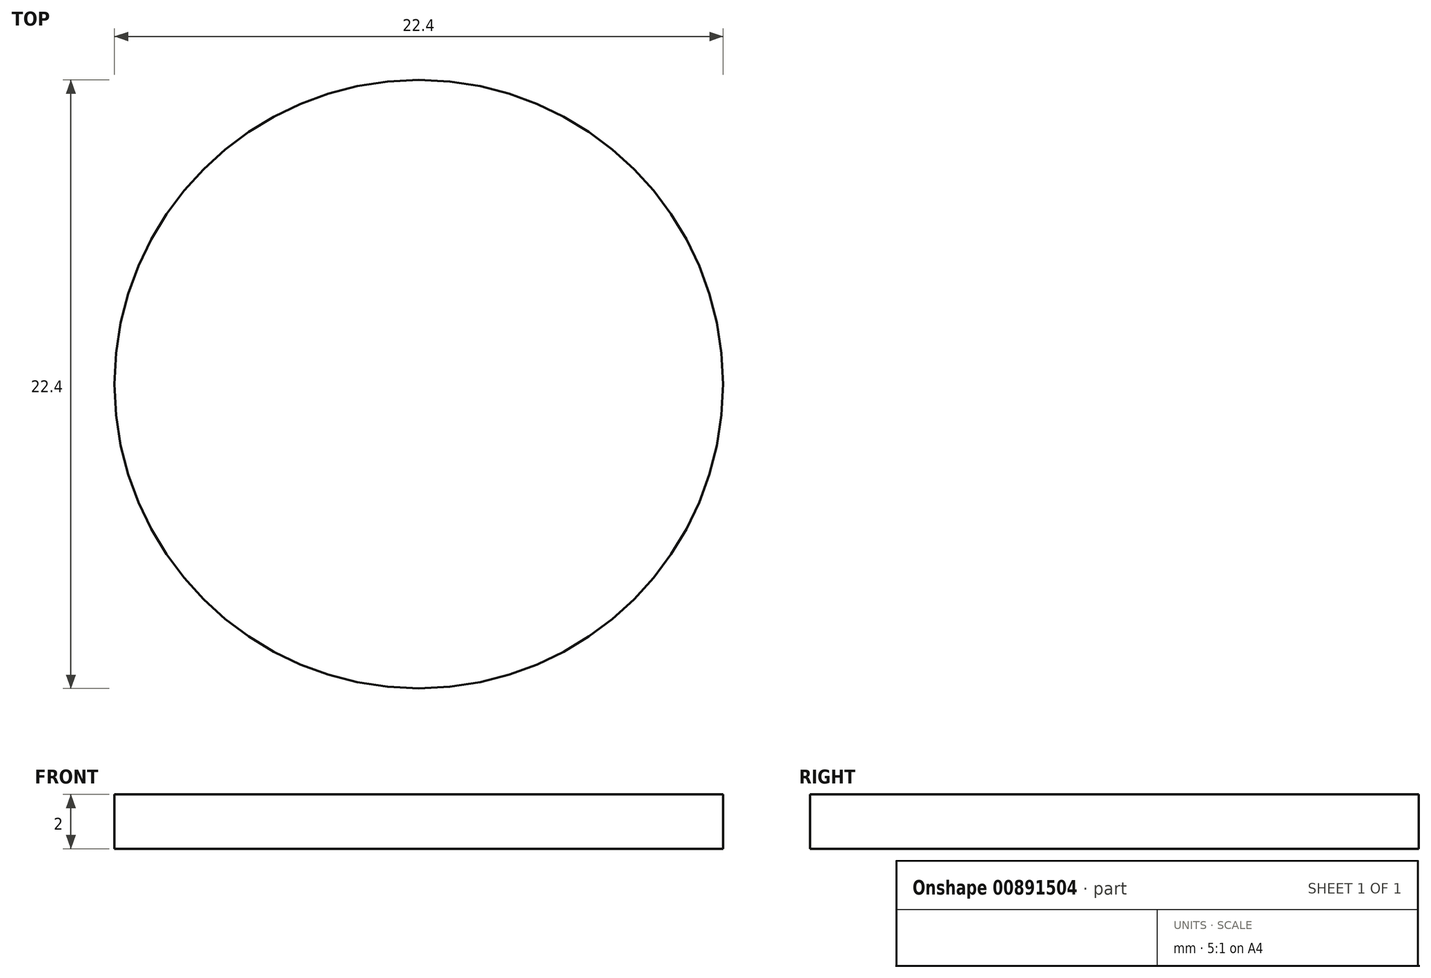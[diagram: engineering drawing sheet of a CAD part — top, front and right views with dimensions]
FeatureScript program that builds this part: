
annotation { "Feature Type Name" : "Feature", "Feature Type Description" : "" }
export const myFeature = defineFeature(function(context is Context, id is Id, definition is map)
    precondition{}
    {
        {
            var Q0;
            Q0=qCreatedBy(makeId("Top.planeOp"),FACE);
            var sketch = newSketch(context, id + "F0", { "sketchPlane" : qUnion([Q0])});
            skCircle(sketch, "E0", {"center": v(0, 0) * mm, "radius": 11.2 * mm});
            skSolve(sketch);
        }
        {
            var Q0;
            Q0 = qSketchRegion(id + "F0", true);
            extrude(context, id + "F1", {"entities" : qUnion([Q0]), "depth" : 2 * mm, "offsetDistance" : 25 * mm});
        }
    });
